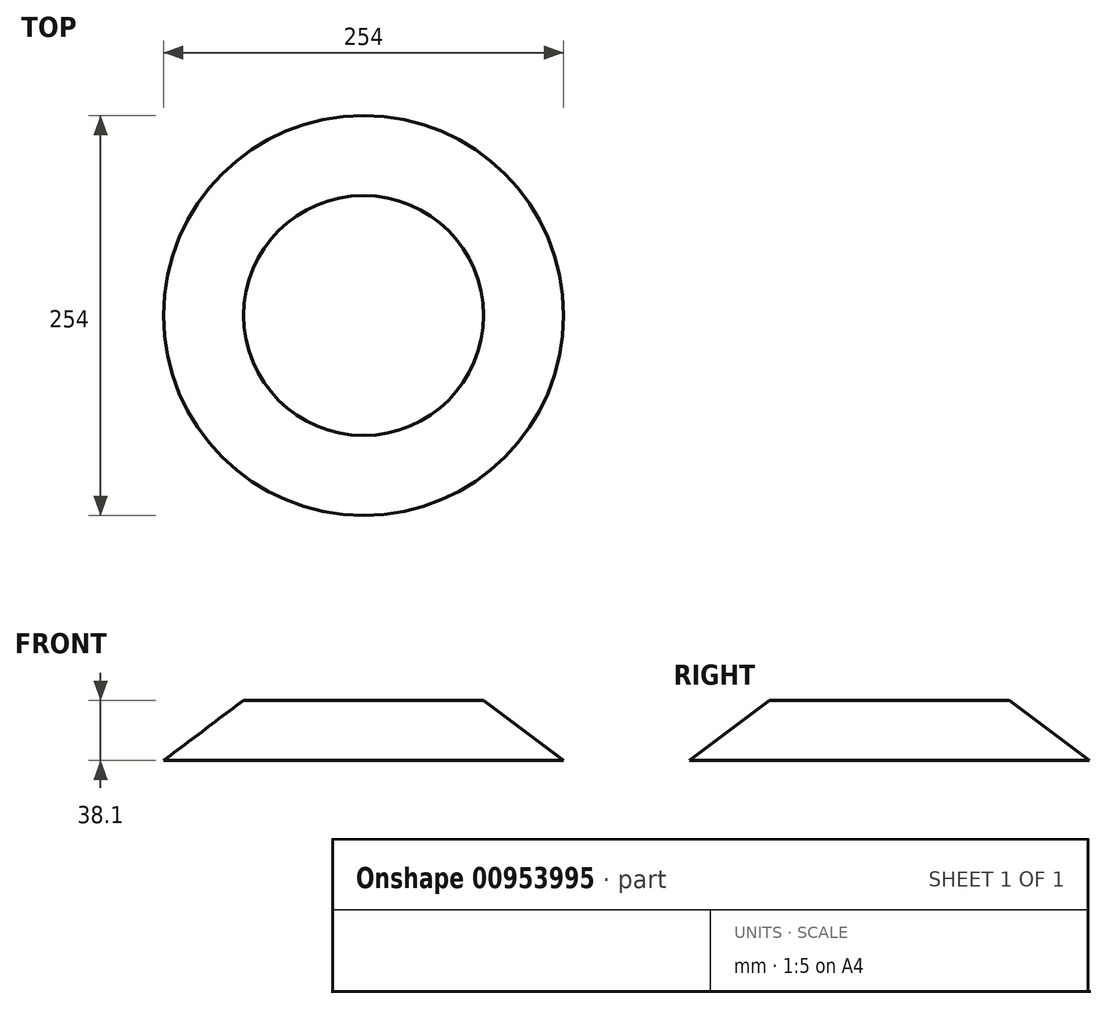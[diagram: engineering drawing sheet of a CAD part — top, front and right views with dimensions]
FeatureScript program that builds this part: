
annotation { "Feature Type Name" : "Feature", "Feature Type Description" : "" }
export const myFeature = defineFeature(function(context is Context, id is Id, definition is map)
    precondition{}
    {
        {
            var Q0;
            Q0=qCreatedBy(makeId("Front.planeOp"),FACE);
            var sketch = newSketch(context, id + "F0", { "sketchPlane" : qUnion([Q0])});
            skLineSegment(sketch, "E0", {"start": v(0, 0) * mm, "end": v(0, 38.1) * mm});
            skLineSegment(sketch, "E1", {"start": v(0, 38.1) * mm, "end": v(76.2, 38.1) * mm});
            skLineSegment(sketch, "E2", {"start": v(0, 0) * mm, "end": v(127, 0) * mm});
            skLineSegment(sketch, "E3", {"start": v(76.2, 38.1) * mm, "end": v(127, 0) * mm});
            skSolve(sketch);
        }
        {
            var Q0;
            Q0=makeQuery(id+"F0.imprint","IMPRINT",FACE,{"disambiguationData":[TD([[makeQuery(id+"F0.imprint","IMPRINT",EDGE,{"derivedFrom":sQuery(id+"F0.wireOp",EDGE,"E0")}),-1.0]])]});
            var Q1;
            Q1=sQuery(id+"F0.wireOp",EDGE,"E0");
            revolve(context, id + "F1", {"surfaceOperationType" : NewSurfaceOperationType.NEW, "entities" : qUnion([Q0]), "axis" : qUnion([Q1]), "revolveType" : RevolveType.FULL});
        }
    });
